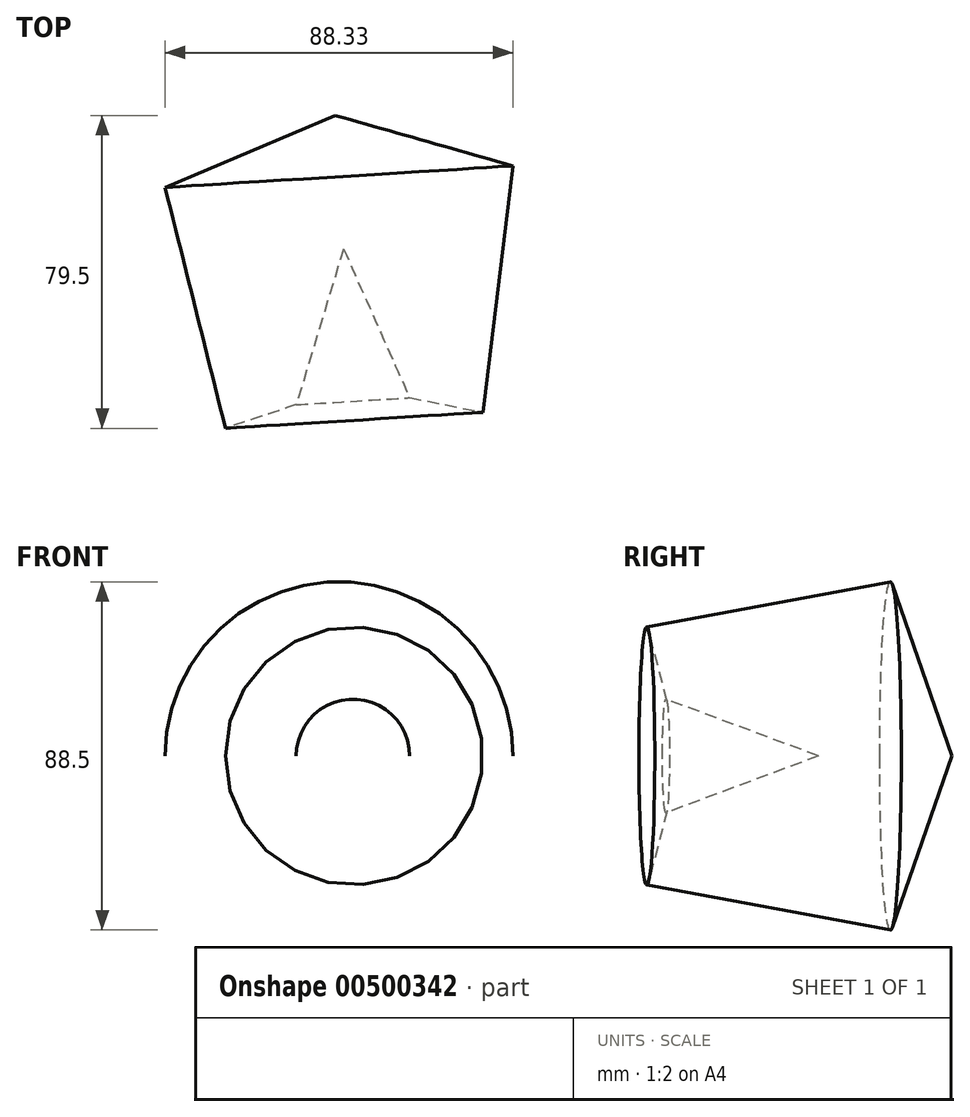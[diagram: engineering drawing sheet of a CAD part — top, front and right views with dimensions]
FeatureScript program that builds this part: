
annotation { "Feature Type Name" : "Feature", "Feature Type Description" : "" }
export const myFeature = defineFeature(function(context is Context, id is Id, definition is map)
    precondition{}
    {
        {
            var Q0;
            Q0=qCreatedBy(makeId("Top.planeOp"),FACE);
            var sketch = newSketch(context, id + "F0", { "sketchPlane" : qUnion([Q0])});
            skLineSegment(sketch, "E0", {"start": v(-25.5, -30.75) * mm, "end": v(-40.8, 30.45) * mm});
            skLineSegment(sketch, "E1", {"start": v(-40.8, 30.45) * mm, "end": v(2.4, 48.75) * mm});
            skLineSegment(sketch, "E2", {"start": v(2.4, 48.75) * mm, "end": v(4.5, 14.85) * mm});
            skLineSegment(sketch, "E3", {"start": v(4.5, 14.85) * mm, "end": v(-7.5, -24.75) * mm});
            skLineSegment(sketch, "E4", {"start": v(-7.5, -24.75) * mm, "end": v(-25.5, -30.75) * mm});
            skSolve(sketch);
        }
        {
            var Q0;
            Q0=makeQuery(id+"F0.imprint","IMPRINT",FACE,{"disambiguationData":[TD([[makeQuery(id+"F0.imprint","IMPRINT",EDGE,{"derivedFrom":sQuery(id+"F0.wireOp",EDGE,"E0")}),-1.0]])]});
            var Q1;
            Q1=sQuery(id+"F0.wireOp",EDGE,"E2");
            revolve(context, id + "F1", {"entities" : qUnion([Q0]), "axis" : qUnion([Q1]), "revolveType" : RevolveType.FULL});
        }
    });
